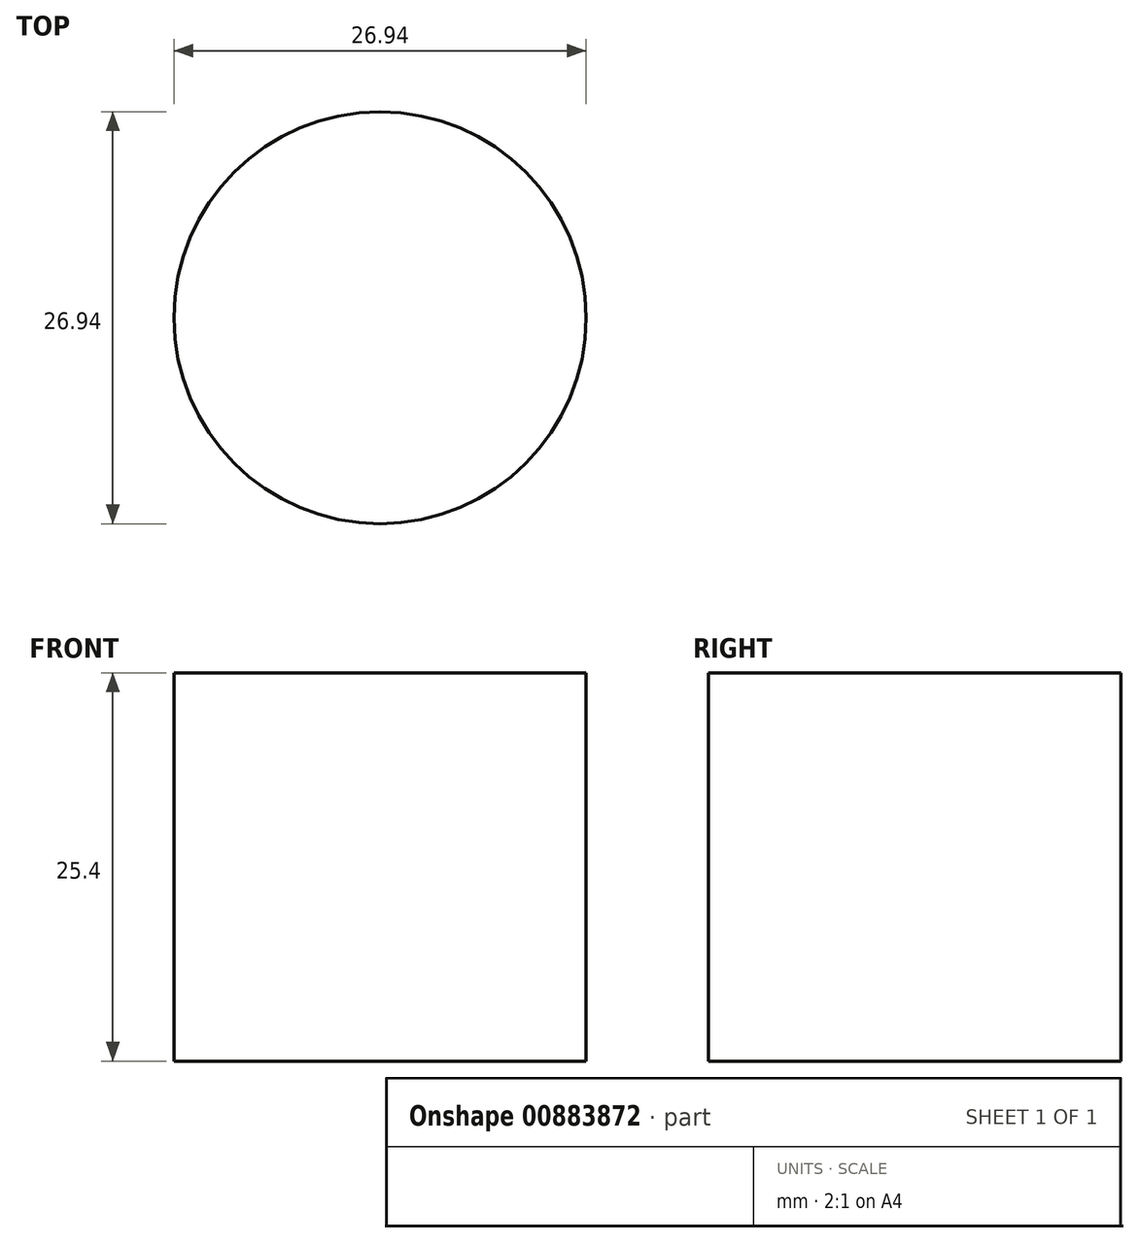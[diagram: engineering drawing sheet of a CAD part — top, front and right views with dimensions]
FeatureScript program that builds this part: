
annotation { "Feature Type Name" : "Feature", "Feature Type Description" : "" }
export const myFeature = defineFeature(function(context is Context, id is Id, definition is map)
    precondition{}
    {
        {
            var Q0;
            Q0=qCreatedBy(makeId("Top.planeOp"),FACE);
            var sketch = newSketch(context, id + "F0", { "sketchPlane" : qUnion([Q0])});
            skLineSegment(sketch, "E0.bottom", {"start": v(-9.52, 9.52) * mm, "end": v(9.53, 9.52) * mm});
            skLineSegment(sketch, "E0.top", {"start": v(-9.53, -9.52) * mm, "end": v(9.52, -9.52) * mm});
            skLineSegment(sketch, "E0.left", {"start": v(-9.52, 9.52) * mm, "end": v(-9.53, -9.52) * mm});
            skLineSegment(sketch, "E0.right", {"start": v(9.53, 9.52) * mm, "end": v(9.52, -9.52) * mm});
            skPoint(sketch, "E0.middle", {"position": v(0, 0) * mm});
            skCircle(sketch, "E1", {"center": v(0, 0) * mm, "radius": 13.47 * mm});
            skSolve(sketch);
        }
        {
            var Q0;
            {var subQ0=sQuery(id+"F0.wireOp",EDGE,"E0.right");Q0=makeQuery(id+"F0.imprint","IMPRINT",FACE,{"disambiguationData":[TD([[makeQuery(id+"F0.imprint","IMPRINT",EDGE,{"derivedFrom":subQ0}),1.0]])]});}
            var Q1;
            {var subQ0=sQuery(id+"F0.wireOp",EDGE,"E0.bottom");Q1=makeQuery(id+"F0.imprint","IMPRINT",FACE,{"disambiguationData":[TD([[makeQuery(id+"F0.imprint","IMPRINT",EDGE,{"derivedFrom":subQ0}),1.0]])]});}
            var Q2;
            {var subQ0=sQuery(id+"F0.wireOp",EDGE,"E0.left");Q2=makeQuery(id+"F0.imprint","IMPRINT",FACE,{"disambiguationData":[TD([[makeQuery(id+"F0.imprint","IMPRINT",EDGE,{"derivedFrom":subQ0}),-1.0]])]});}
            var Q3;
            {var subQ0=sQuery(id+"F0.wireOp",EDGE,"E0.top");Q3=makeQuery(id+"F0.imprint","IMPRINT",FACE,{"disambiguationData":[TD([[makeQuery(id+"F0.imprint","IMPRINT",EDGE,{"derivedFrom":subQ0}),-1.0]])]});}
            var Q4;
            Q4=makeQuery(id+"F0.imprint","IMPRINT",FACE,{"disambiguationData":[TD([[makeQuery(id+"F0.imprint","IMPRINT",EDGE,{"derivedFrom":sQuery(id+"F0.wireOp",EDGE,"E0.bottom")}),-1.0]])]});
            extrude(context, id + "F1", {"entities" : qUnion([Q0, Q1, Q2, Q3, Q4]), "depth" : 25.4 * mm, "offsetDistance" : 25.4 * mm});
        }
    });
